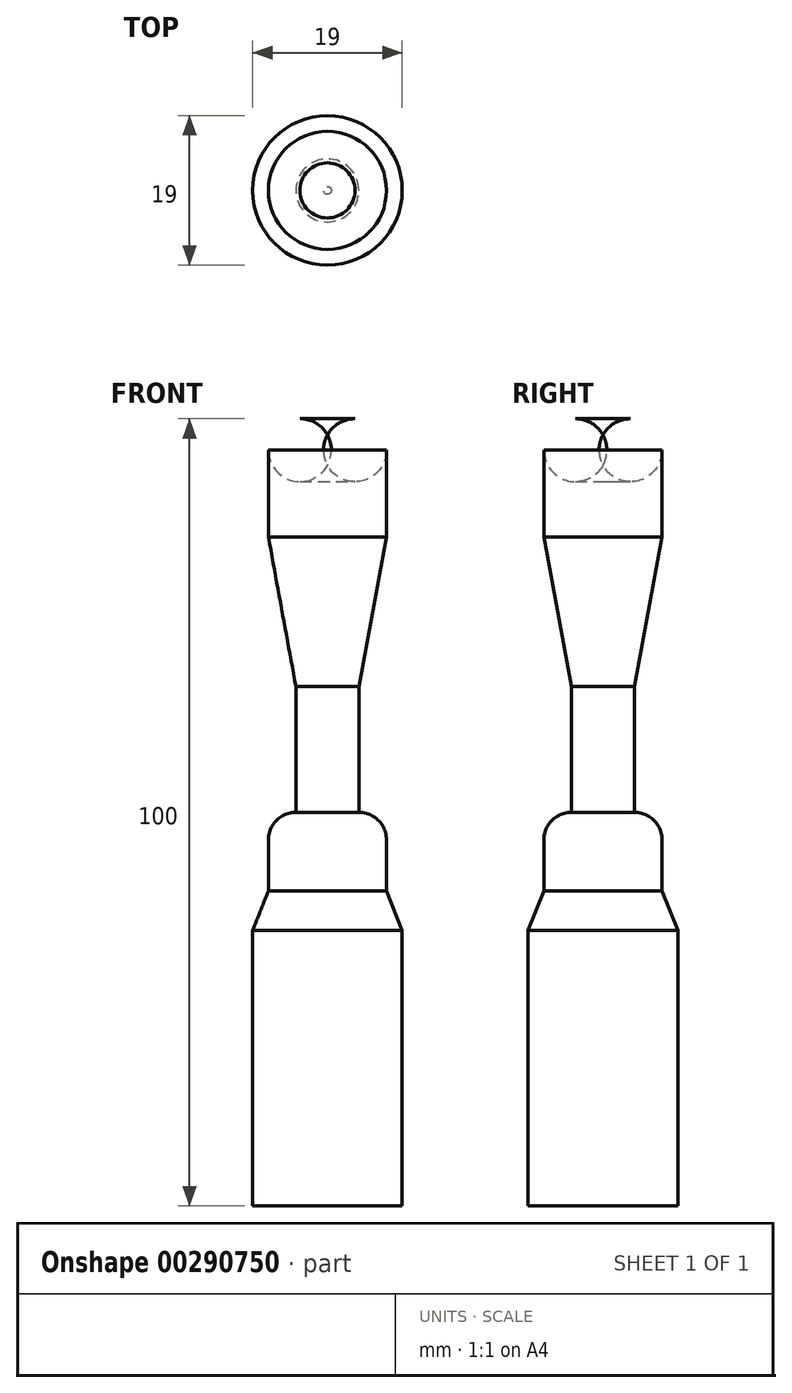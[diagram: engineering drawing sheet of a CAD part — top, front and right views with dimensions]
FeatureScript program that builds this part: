
annotation { "Feature Type Name" : "Feature", "Feature Type Description" : "" }
export const myFeature = defineFeature(function(context is Context, id is Id, definition is map)
    precondition{}
    {
        {
            var Q0;
            Q0=qCreatedBy(makeId("Front.planeOp"),FACE);
            var sketch = newSketch(context, id + "F0", { "sketchPlane" : qUnion([Q0])});
            skLineSegment(sketch, "E0", {"start": v(0, 0) * mm, "end": v(3.5, 0) * mm});
            skArc(sketch, "E1", {"start": v(7.5, -4) * mm, "mid": v(6.33, -1.17) * mm, "end": v(3.5, 0) * mm});
            skLineSegment(sketch, "E2", {"start": v(7.5, -4) * mm, "end": v(7.5, -15) * mm});
            skLineSegment(sketch, "E3", {"start": v(7.5, -15) * mm, "end": v(4, -34) * mm});
            skLineSegment(sketch, "E4", {"start": v(4, -34) * mm, "end": v(4, -50) * mm});
            skArc(sketch, "E5", {"start": v(7.5, -53.5) * mm, "mid": v(6.47, -51.03) * mm, "end": v(4, -50) * mm});
            skLineSegment(sketch, "E6", {"start": v(7.5, -53.5) * mm, "end": v(7.5, -60) * mm});
            skLineSegment(sketch, "E7", {"start": v(7.5, -60) * mm, "end": v(9.5, -65) * mm});
            skLineSegment(sketch, "E8", {"start": v(9.5, -65) * mm, "end": v(9.5, -100) * mm});
            skLineSegment(sketch, "E9", {"start": v(9.5, -100) * mm, "end": v(0, -100) * mm});
            skLineSegment(sketch, "E10", {"start": v(0, -100) * mm, "end": v(0, 0) * mm});
            skSolve(sketch);
        }
        {
            var Q0;
            Q0 = qSketchRegion(id + "F0", true);
            var Q1;
            Q1=sQuery(id+"F0.wireOp",EDGE,"E10");
            revolve(context, id + "F1", {"entities" : qUnion([Q0]), "axis" : qUnion([Q1]), "revolveType" : RevolveType.FULL});
        }
    });
